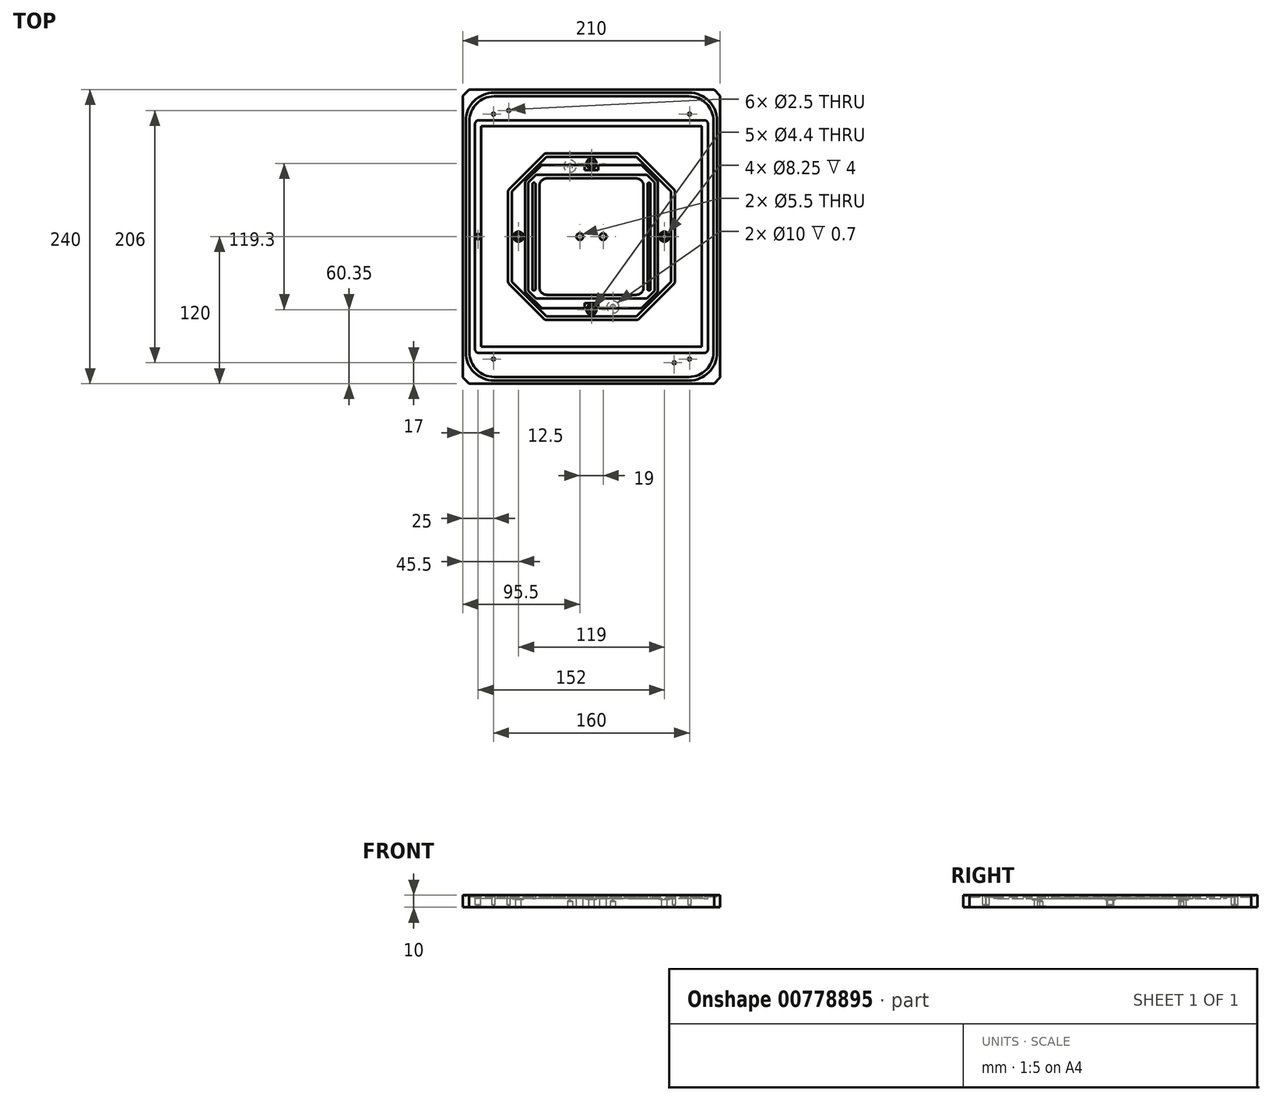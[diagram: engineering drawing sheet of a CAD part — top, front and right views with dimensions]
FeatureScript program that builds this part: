
annotation { "Feature Type Name" : "Feature", "Feature Type Description" : "" }
export const myFeature = defineFeature(function(context is Context, id is Id, definition is map)
    precondition{}
    {
        {
            var Q0;
            Q0=qCreatedBy(makeId("Top.planeOp"),FACE);
            var sketch = newSketch(context, id + "F0", { "sketchPlane" : qUnion([Q0])});
            skLineSegment(sketch, "E0.bottom", {"start": v(105, -120) * mm, "end": v(-105, -120) * mm});
            skLineSegment(sketch, "E0.top", {"start": v(105, 120) * mm, "end": v(-105, 120) * mm});
            skLineSegment(sketch, "E0.left", {"start": v(105, -120) * mm, "end": v(105, 120) * mm});
            skLineSegment(sketch, "E0.right", {"start": v(-105, -120) * mm, "end": v(-105, 120) * mm});
            skPoint(sketch, "E0.middle", {"position": v(0, 0) * mm});
            skSolve(sketch);
        }
        {
            var Q0;
            Q0 = qSketchRegion(id + "F0", true);
            extrude(context, id + "F1", {"entities" : qUnion([Q0]), "depth" : 10 * mm, "offsetDistance" : 25 * mm});
        }
        {
            var Q0;
            Q0=makeQuery(id+"F1.opExtrude","CAP_FACE",FACE,{"disambiguationData":[OSD([sQuery(id+"F0.wireOp",EDGE,"E0.bottom"),sQuery(id+"F0.wireOp",EDGE,"E0.top"),sQuery(id+"F0.wireOp",EDGE,"E0.left"),sQuery(id+"F0.wireOp",EDGE,"E0.right")])],"isStart":false});
            var sketch = newSketch(context, id + "F2", { "sketchPlane" : qUnion([Q0])});
            skPoint(sketch, "E1.middle", {"position": v(0, 0) * mm});
            skLineSegment(sketch, "E2.bottom", {"start": v(79.5, -114.5) * mm, "end": v(-79.5, -114.5) * mm});
            skLineSegment(sketch, "E2.top", {"start": v(79.5, 114.5) * mm, "end": v(-79.5, 114.5) * mm});
            skLineSegment(sketch, "E2.left", {"start": v(99.5, -94.5) * mm, "end": v(99.5, 94.5) * mm});
            skLineSegment(sketch, "E2.right", {"start": v(-99.5, -94.5) * mm, "end": v(-99.5, 94.5) * mm});
            skPoint(sketch, "E3.visualSharp", {"position": v(99.5, 114.5) * mm});
            skArc(sketch, "E3.filletArc", {"start": v(99.5, 94.5) * mm, "mid": v(93.64, 108.64) * mm, "end": v(79.5, 114.5) * mm});
            skPoint(sketch, "E4.visualSharp", {"position": v(-99.5, 114.5) * mm});
            skArc(sketch, "E4.filletArc", {"start": v(-79.5, 114.5) * mm, "mid": v(-93.64, 108.64) * mm, "end": v(-99.5, 94.5) * mm});
            skPoint(sketch, "E5.visualSharp", {"position": v(-99.5, -114.5) * mm});
            skArc(sketch, "E5.filletArc", {"start": v(-99.5, -94.5) * mm, "mid": v(-93.64, -108.64) * mm, "end": v(-79.5, -114.5) * mm});
            skPoint(sketch, "E6.visualSharp", {"position": v(99.5, -114.5) * mm});
            skArc(sketch, "E6.filletArc", {"start": v(79.5, -114.5) * mm, "mid": v(93.64, -108.64) * mm, "end": v(99.5, -94.5) * mm});
            skArc(sketch, "E7.0", {"start": v(102.5, 94.5) * mm, "mid": v(95.76, 110.76) * mm, "end": v(79.5, 117.5) * mm});
            skLineSegment(sketch, "E7.1", {"start": v(102.5, -94.5) * mm, "end": v(102.5, 94.5) * mm});
            skLineSegment(sketch, "E7.2", {"start": v(79.5, 117.5) * mm, "end": v(-79.5, 117.5) * mm});
            skArc(sketch, "E7.3", {"start": v(79.5, -117.5) * mm, "mid": v(95.76, -110.76) * mm, "end": v(102.5, -94.5) * mm});
            skArc(sketch, "E7.4", {"start": v(-79.5, 117.5) * mm, "mid": v(-95.76, 110.76) * mm, "end": v(-102.5, 94.5) * mm});
            skLineSegment(sketch, "E7.5", {"start": v(-102.5, -94.5) * mm, "end": v(-102.5, 94.5) * mm});
            skArc(sketch, "E7.6", {"start": v(-102.5, -94.5) * mm, "mid": v(-95.76, -110.76) * mm, "end": v(-79.5, -117.5) * mm});
            skLineSegment(sketch, "E7.7", {"start": v(79.5, -117.5) * mm, "end": v(-79.5, -117.5) * mm});
            skSolve(sketch);
        }
        {
            var Q0;
            Q0 = qSketchRegion(id + "F2", true);
            extrude(context, id + "F3", {"entities" : qUnion([Q0]), "operationType" : NewBodyOperationType.REMOVE, "oppositeDirection" : true, "depth" : 1.5 * mm, "offsetDistance" : 25 * mm});
        }
        {
            var Q0;
            Q0=makeQuery(id+"F3.boolean.opBoolean","SPLIT",FACE,{"disambiguationData":[TD([makeQuery(id+"F3.opExtrude","SWEPT_FACE",FACE,{"disambiguationData":[OSD([sQuery(id+"F2.wireOp",EDGE,"E2.bottom")])]})])],"derivedFrom":makeQuery(id+"F1.opExtrude","CAP_FACE",FACE,{"disambiguationData":[OSD([sQuery(id+"F0.wireOp",EDGE,"E0.bottom"),sQuery(id+"F0.wireOp",EDGE,"E0.top"),sQuery(id+"F0.wireOp",EDGE,"E0.left"),sQuery(id+"F0.wireOp",EDGE,"E0.right")])],"isStart":false})});
            var sketch = newSketch(context, id + "F4", { "sketchPlane" : qUnion([Q0])});
            skLineSegment(sketch, "E8.bottom", {"start": v(90, -90) * mm, "end": v(-90, -90) * mm});
            skLineSegment(sketch, "E8.top", {"start": v(90, 90) * mm, "end": v(-90, 90) * mm});
            skLineSegment(sketch, "E8.left", {"start": v(90, -90) * mm, "end": v(90, 90) * mm});
            skLineSegment(sketch, "E8.right", {"start": v(-90, -90) * mm, "end": v(-90, 90) * mm});
            skPoint(sketch, "E8.middle", {"position": v(0, 0) * mm});
            skLineSegment(sketch, "E9.0", {"start": v(92, 95) * mm, "end": v(-92, 95) * mm});
            skLineSegment(sketch, "E9.1", {"start": v(95, -92) * mm, "end": v(95, 92) * mm});
            skLineSegment(sketch, "E9.2", {"start": v(92, -95) * mm, "end": v(-92, -95) * mm});
            skLineSegment(sketch, "E9.3", {"start": v(-95, -92) * mm, "end": v(-95, 92) * mm});
            skPoint(sketch, "E10.visualSharp", {"position": v(95, 95) * mm});
            skArc(sketch, "E10.filletArc", {"start": v(95, 92) * mm, "mid": v(94.12, 94.12) * mm, "end": v(92, 95) * mm});
            skPoint(sketch, "E11.visualSharp", {"position": v(-95, 95) * mm});
            skArc(sketch, "E11.filletArc", {"start": v(-92, 95) * mm, "mid": v(-94.12, 94.12) * mm, "end": v(-95, 92) * mm});
            skPoint(sketch, "E12.visualSharp", {"position": v(-95, -95) * mm});
            skArc(sketch, "E12.filletArc", {"start": v(-95, -92) * mm, "mid": v(-94.12, -94.12) * mm, "end": v(-92, -95) * mm});
            skPoint(sketch, "E13.visualSharp", {"position": v(95, -95) * mm});
            skArc(sketch, "E13.filletArc", {"start": v(92, -95) * mm, "mid": v(94.12, -94.12) * mm, "end": v(95, -92) * mm});
            skSolve(sketch);
        }
        {
            var Q0;
            Q0 = qSketchRegion(id + "F4", true);
            extrude(context, id + "F5", {"entities" : qUnion([Q0]), "operationType" : NewBodyOperationType.REMOVE, "oppositeDirection" : true, "depth" : 3 * mm, "offsetDistance" : 25 * mm});
        }
        {
            var Q0;
            Q0=makeQuery(id+"F5.boolean.opBoolean","SPLIT",FACE,{"disambiguationData":[TD([makeQuery(id+"F5.opExtrude","SWEPT_FACE",FACE,{"disambiguationData":[OSD([sQuery(id+"F4.wireOp",EDGE,"E8.bottom")])]})])],"derivedFrom":makeQuery(id+"F3.boolean.opBoolean","SPLIT",FACE,{"disambiguationData":[TD([makeQuery(id+"F3.opExtrude","SWEPT_FACE",FACE,{"disambiguationData":[OSD([sQuery(id+"F2.wireOp",EDGE,"E2.bottom")])]})])],"derivedFrom":makeQuery(id+"F1.opExtrude","CAP_FACE",FACE,{"disambiguationData":[OSD([sQuery(id+"F0.wireOp",EDGE,"E0.bottom"),sQuery(id+"F0.wireOp",EDGE,"E0.top"),sQuery(id+"F0.wireOp",EDGE,"E0.left"),sQuery(id+"F0.wireOp",EDGE,"E0.right")])],"isStart":false})})});
            var sketch = newSketch(context, id + "F6", { "sketchPlane" : qUnion([Q0])});
            skLineSegment(sketch, "E14", {"start": v(-90, 0) * mm, "end": v(90, 0) * mm, "construction": true});
            skLineSegment(sketch, "E15", {"start": v(0, 90) * mm, "end": v(0, -90) * mm, "construction": true});
            skLineSegment(sketch, "E16", {"start": v(-65, 0) * mm, "end": v(-65, 36.72) * mm});
            skLineSegment(sketch, "E17", {"start": v(-65, 36.72) * mm, "end": v(-36.72, 65) * mm});
            skLineSegment(sketch, "E18", {"start": v(-36.72, 65) * mm, "end": v(0, 65) * mm});
            skLineSegment(sketch, "E19.MirrorCS", {"start": v(65, 0) * mm, "end": v(65, 36.72) * mm});
            skLineSegment(sketch, "E20.MirrorCS", {"start": v(36.72, 65) * mm, "end": v(0, 65) * mm});
            skLineSegment(sketch, "E21.MirrorCS", {"start": v(65, 36.72) * mm, "end": v(36.72, 65) * mm});
            skLineSegment(sketch, "E22.MirrorCS", {"start": v(65, 0) * mm, "end": v(65, -36.72) * mm});
            skLineSegment(sketch, "E23.MirrorCS", {"start": v(65, -36.72) * mm, "end": v(36.72, -65) * mm});
            skLineSegment(sketch, "E24.MirrorCS", {"start": v(36.72, -65) * mm, "end": v(0, -65) * mm});
            skLineSegment(sketch, "E25.MirrorCS", {"start": v(-36.72, -65) * mm, "end": v(0, -65) * mm});
            skLineSegment(sketch, "E26.MirrorCS", {"start": v(-65, -36.72) * mm, "end": v(-36.72, -65) * mm});
            skLineSegment(sketch, "E27.MirrorCS", {"start": v(-65, 0) * mm, "end": v(-65, -36.72) * mm});
            skLineSegment(sketch, "E28.0", {"start": v(67.12, 38.84) * mm, "end": v(38.84, 67.12) * mm});
            skLineSegment(sketch, "E28.1", {"start": v(-68, 0) * mm, "end": v(-68, -36.72) * mm});
            skLineSegment(sketch, "E28.2", {"start": v(-68, 0) * mm, "end": v(-68, 36.72) * mm});
            skLineSegment(sketch, "E28.3", {"start": v(-67.12, 38.84) * mm, "end": v(-38.84, 67.12) * mm});
            skLineSegment(sketch, "E28.4", {"start": v(-36.72, 68) * mm, "end": v(0, 68) * mm});
            skLineSegment(sketch, "E28.5", {"start": v(-67.12, -38.84) * mm, "end": v(-38.84, -67.12) * mm});
            skLineSegment(sketch, "E28.6", {"start": v(36.72, 68) * mm, "end": v(0, 68) * mm});
            skLineSegment(sketch, "E28.7", {"start": v(-36.72, -68) * mm, "end": v(0, -68) * mm});
            skLineSegment(sketch, "E28.8", {"start": v(36.72, -68) * mm, "end": v(0, -68) * mm});
            skLineSegment(sketch, "E28.9", {"start": v(67.12, -38.84) * mm, "end": v(38.84, -67.12) * mm});
            skLineSegment(sketch, "E28.10", {"start": v(68, 0) * mm, "end": v(68, -36.72) * mm});
            skLineSegment(sketch, "E28.11", {"start": v(68, 0) * mm, "end": v(68, 36.72) * mm});
            skPoint(sketch, "E29.visualSharp", {"position": v(37.96, 68) * mm});
            skArc(sketch, "E29.filletArc", {"start": v(38.84, 67.12) * mm, "mid": v(37.86, 67.77) * mm, "end": v(36.72, 68) * mm});
            skPoint(sketch, "E30.visualSharp", {"position": v(-37.96, 68) * mm});
            skArc(sketch, "E30.filletArc", {"start": v(-36.72, 68) * mm, "mid": v(-37.86, 67.77) * mm, "end": v(-38.84, 67.12) * mm});
            skPoint(sketch, "E31.visualSharp", {"position": v(-68, 37.96) * mm});
            skArc(sketch, "E31.filletArc", {"start": v(-67.12, 38.84) * mm, "mid": v(-67.77, 37.86) * mm, "end": v(-68, 36.72) * mm});
            skPoint(sketch, "E32.visualSharp", {"position": v(68, 37.96) * mm});
            skArc(sketch, "E32.filletArc", {"start": v(68, 36.72) * mm, "mid": v(67.77, 37.86) * mm, "end": v(67.12, 38.84) * mm});
            skPoint(sketch, "E33.visualSharp", {"position": v(-68, -37.96) * mm});
            skArc(sketch, "E33.filletArc", {"start": v(-68, -36.72) * mm, "mid": v(-67.77, -37.86) * mm, "end": v(-67.12, -38.84) * mm});
            skPoint(sketch, "E34.visualSharp", {"position": v(-37.96, -68) * mm});
            skArc(sketch, "E34.filletArc", {"start": v(-38.84, -67.12) * mm, "mid": v(-37.86, -67.77) * mm, "end": v(-36.72, -68) * mm});
            skPoint(sketch, "E35.visualSharp", {"position": v(37.96, -68) * mm});
            skArc(sketch, "E35.filletArc", {"start": v(36.72, -68) * mm, "mid": v(37.86, -67.77) * mm, "end": v(38.84, -67.12) * mm});
            skPoint(sketch, "E36.visualSharp", {"position": v(68, -37.96) * mm});
            skArc(sketch, "E36.filletArc", {"start": v(67.12, -38.84) * mm, "mid": v(67.77, -37.86) * mm, "end": v(68, -36.72) * mm});
            skSolve(sketch);
        }
        {
            var Q0;
            Q0 = qSketchRegion(id + "F6", true);
            var Q1;
            Q1=makeQuery(id+"F5.boolean.opBoolean","COPY",FACE,{"derivedFrom":makeQuery(id+"F5.opExtrude","CAP_FACE",FACE,{"disambiguationData":[OSD([sQuery(id+"F4.wireOp",EDGE,"E8.bottom"),sQuery(id+"F4.wireOp",EDGE,"E8.top"),sQuery(id+"F4.wireOp",EDGE,"E8.left"),sQuery(id+"F4.wireOp",EDGE,"E8.right"),sQuery(id+"F4.wireOp",EDGE,"E9.0"),sQuery(id+"F4.wireOp",EDGE,"E9.1"),sQuery(id+"F4.wireOp",EDGE,"E9.2"),sQuery(id+"F4.wireOp",EDGE,"E9.3"),sQuery(id+"F4.wireOp",EDGE,"E10.filletArc"),sQuery(id+"F4.wireOp",EDGE,"E11.filletArc"),sQuery(id+"F4.wireOp",EDGE,"E12.filletArc"),sQuery(id+"F4.wireOp",EDGE,"E13.filletArc")])],"isStart":false})});
            extrude(context, id + "F7", {"entities" : qUnion([Q0]), "operationType" : NewBodyOperationType.REMOVE, "endBound" : BoundingType.UP_TO_SURFACE, "oppositeDirection" : true, "depth" : 25 * mm, "endBoundEntityFace" : qUnion([Q1]), "offsetDistance" : 25 * mm});
        }
        {
            var Q0;
            Q0=makeQuery(id+"F7.boolean.opBoolean","SPLIT",FACE,{"disambiguationData":[TD([makeQuery(id+"F7.opExtrude","SWEPT_FACE",FACE,{"disambiguationData":[OSD([sQuery(id+"F6.wireOp",EDGE,"E17")])]})])],"derivedFrom":makeQuery(id+"F5.boolean.opBoolean","SPLIT",FACE,{"disambiguationData":[TD([makeQuery(id+"F5.opExtrude","SWEPT_FACE",FACE,{"disambiguationData":[OSD([sQuery(id+"F4.wireOp",EDGE,"E8.bottom")])]})])],"derivedFrom":makeQuery(id+"F3.boolean.opBoolean","SPLIT",FACE,{"disambiguationData":[TD([makeQuery(id+"F3.opExtrude","SWEPT_FACE",FACE,{"disambiguationData":[OSD([sQuery(id+"F2.wireOp",EDGE,"E2.bottom")])]})])],"derivedFrom":makeQuery(id+"F1.opExtrude","CAP_FACE",FACE,{"disambiguationData":[OSD([sQuery(id+"F0.wireOp",EDGE,"E0.bottom"),sQuery(id+"F0.wireOp",EDGE,"E0.top"),sQuery(id+"F0.wireOp",EDGE,"E0.left"),sQuery(id+"F0.wireOp",EDGE,"E0.right")])],"isStart":false})})})});
            var sketch = newSketch(context, id + "F8", { "sketchPlane" : qUnion([Q0])});
            skLineSegment(sketch, "E37", {"start": v(-65, 0) * mm, "end": v(65, 0) * mm, "construction": true});
            skLineSegment(sketch, "E38", {"start": v(0, 65) * mm, "end": v(0, -65) * mm, "construction": true});
            skLineSegment(sketch, "E39", {"start": v(-51.5, 0) * mm, "end": v(-51.5, 44.14) * mm});
            skLineSegment(sketch, "E40", {"start": v(-51.5, 44.14) * mm, "end": v(-45.14, 50.5) * mm});
            skLineSegment(sketch, "E41", {"start": v(-45.14, 50.5) * mm, "end": v(0, 50.5) * mm});
            skLineSegment(sketch, "E42", {"start": v(-54, 0) * mm, "end": v(-54, 45.17) * mm});
            skLineSegment(sketch, "E43", {"start": v(-54, 45.17) * mm, "end": v(-40.67, 58.5) * mm});
            skLineSegment(sketch, "E44", {"start": v(-40.67, 58.5) * mm, "end": v(-5.5, 58.5) * mm});
            skLineSegment(sketch, "E45", {"start": v(-5.5, 58.5) * mm, "end": v(-5.5, 54.3) * mm});
            skLineSegment(sketch, "E46", {"start": v(-5.5, 54.3) * mm, "end": v(0, 54.3) * mm});
            skLineSegment(sketch, "E47.MirrorCS", {"start": v(5.5, 54.3) * mm, "end": v(0, 54.3) * mm});
            skLineSegment(sketch, "E48.MirrorCS", {"start": v(5.5, 58.5) * mm, "end": v(5.5, 54.3) * mm});
            skLineSegment(sketch, "E49.MirrorCS", {"start": v(40.67, 58.5) * mm, "end": v(5.5, 58.5) * mm});
            skLineSegment(sketch, "E50.MirrorCS", {"start": v(45.14, 50.5) * mm, "end": v(0, 50.5) * mm});
            skLineSegment(sketch, "E51.MirrorCS", {"start": v(54, 45.17) * mm, "end": v(40.67, 58.5) * mm});
            skLineSegment(sketch, "E52.MirrorCS", {"start": v(51.5, 44.14) * mm, "end": v(45.14, 50.5) * mm});
            skLineSegment(sketch, "E53.MirrorCS", {"start": v(54, 0) * mm, "end": v(54, 45.17) * mm});
            skLineSegment(sketch, "E54.MirrorCS", {"start": v(51.5, 0) * mm, "end": v(51.5, 44.14) * mm});
            skLineSegment(sketch, "E55.MirrorCS", {"start": v(54, 0) * mm, "end": v(54, -45.17) * mm});
            skLineSegment(sketch, "E56.MirrorCS", {"start": v(51.5, 0) * mm, "end": v(51.5, -44.14) * mm});
            skLineSegment(sketch, "E57.MirrorCS", {"start": v(51.5, -44.14) * mm, "end": v(45.14, -50.5) * mm});
            skLineSegment(sketch, "E58.MirrorCS", {"start": v(54, -45.17) * mm, "end": v(40.67, -58.5) * mm});
            skLineSegment(sketch, "E59.MirrorCS", {"start": v(40.67, -58.5) * mm, "end": v(5.5, -58.5) * mm});
            skLineSegment(sketch, "E60.MirrorCS", {"start": v(45.14, -50.5) * mm, "end": v(0, -50.5) * mm});
            skLineSegment(sketch, "E61.MirrorCS", {"start": v(5.5, -58.5) * mm, "end": v(5.5, -54.3) * mm});
            skLineSegment(sketch, "E62.MirrorCS", {"start": v(5.5, -54.3) * mm, "end": v(0, -54.3) * mm});
            skLineSegment(sketch, "E63.MirrorCS", {"start": v(-5.5, -54.3) * mm, "end": v(0, -54.3) * mm});
            skLineSegment(sketch, "E64.MirrorCS", {"start": v(-5.5, -58.5) * mm, "end": v(-5.5, -54.3) * mm});
            skLineSegment(sketch, "E65.MirrorCS", {"start": v(-40.67, -58.5) * mm, "end": v(-5.5, -58.5) * mm});
            skLineSegment(sketch, "E66.MirrorCS", {"start": v(-45.14, -50.5) * mm, "end": v(0, -50.5) * mm});
            skLineSegment(sketch, "E67.MirrorCS", {"start": v(-54, -45.17) * mm, "end": v(-40.67, -58.5) * mm});
            skLineSegment(sketch, "E68.MirrorCS", {"start": v(-51.5, -44.14) * mm, "end": v(-45.14, -50.5) * mm});
            skLineSegment(sketch, "E69.MirrorCS", {"start": v(-54, 0) * mm, "end": v(-54, -45.17) * mm});
            skLineSegment(sketch, "E70.MirrorCS", {"start": v(-51.5, 0) * mm, "end": v(-51.5, -44.14) * mm});
            skSolve(sketch);
        }
        {
            var Q0;
            Q0 = qSketchRegion(id + "F8", true);
            var Q1;
            Q1=makeQuery(id+"F5.boolean.opBoolean","COPY",FACE,{"derivedFrom":makeQuery(id+"F5.opExtrude","CAP_FACE",FACE,{"disambiguationData":[OSD([sQuery(id+"F4.wireOp",EDGE,"E8.bottom"),sQuery(id+"F4.wireOp",EDGE,"E8.top"),sQuery(id+"F4.wireOp",EDGE,"E8.left"),sQuery(id+"F4.wireOp",EDGE,"E8.right"),sQuery(id+"F4.wireOp",EDGE,"E9.0"),sQuery(id+"F4.wireOp",EDGE,"E9.1"),sQuery(id+"F4.wireOp",EDGE,"E9.2"),sQuery(id+"F4.wireOp",EDGE,"E9.3"),sQuery(id+"F4.wireOp",EDGE,"E10.filletArc"),sQuery(id+"F4.wireOp",EDGE,"E11.filletArc"),sQuery(id+"F4.wireOp",EDGE,"E12.filletArc"),sQuery(id+"F4.wireOp",EDGE,"E13.filletArc")])],"isStart":false})});
            extrude(context, id + "F9", {"entities" : qUnion([Q0]), "operationType" : NewBodyOperationType.REMOVE, "endBound" : BoundingType.UP_TO_SURFACE, "oppositeDirection" : true, "depth" : 25 * mm, "endBoundEntityFace" : qUnion([Q1]), "offsetDistance" : 25 * mm});
        }
        {
            var Q0;
            Q0=makeQuery(id+"F9.boolean.opBoolean","SPLIT",FACE,{"disambiguationData":[TD([makeQuery(id+"F9.opExtrude","SWEPT_FACE",FACE,{"disambiguationData":[OSD([sQuery(id+"F8.wireOp",EDGE,"E40")])]})])],"derivedFrom":makeQuery(id+"F7.boolean.opBoolean","SPLIT",FACE,{"disambiguationData":[TD([makeQuery(id+"F7.opExtrude","SWEPT_FACE",FACE,{"disambiguationData":[OSD([sQuery(id+"F6.wireOp",EDGE,"E17")])]})])],"derivedFrom":makeQuery(id+"F5.boolean.opBoolean","SPLIT",FACE,{"disambiguationData":[TD([makeQuery(id+"F5.opExtrude","SWEPT_FACE",FACE,{"disambiguationData":[OSD([sQuery(id+"F4.wireOp",EDGE,"E8.bottom")])]})])],"derivedFrom":makeQuery(id+"F3.boolean.opBoolean","SPLIT",FACE,{"disambiguationData":[TD([makeQuery(id+"F3.opExtrude","SWEPT_FACE",FACE,{"disambiguationData":[OSD([sQuery(id+"F2.wireOp",EDGE,"E2.bottom")])]})])],"derivedFrom":makeQuery(id+"F1.opExtrude","CAP_FACE",FACE,{"disambiguationData":[OSD([sQuery(id+"F0.wireOp",EDGE,"E0.bottom"),sQuery(id+"F0.wireOp",EDGE,"E0.top"),sQuery(id+"F0.wireOp",EDGE,"E0.left"),sQuery(id+"F0.wireOp",EDGE,"E0.right")])],"isStart":false})})})})});
            var sketch = newSketch(context, id + "F10", { "sketchPlane" : qUnion([Q0])});
            skLineSegment(sketch, "E71", {"start": v(0, 50.5) * mm, "end": v(0, -50.5) * mm, "construction": true});
            skLineSegment(sketch, "E72.left", {"start": v(-48.2, 42.75) * mm, "end": v(-48.2, -42.75) * mm});
            skLineSegment(sketch, "E72.right", {"start": v(-45.7, 42.75) * mm, "end": v(-45.7, -42.75) * mm});
            skArc(sketch, "E73", {"start": v(-45.7, 42.75) * mm, "mid": v(-46.95, 44) * mm, "end": v(-48.2, 42.75) * mm});
            skArc(sketch, "E74", {"start": v(-48.2, -42.75) * mm, "mid": v(-46.95, -44) * mm, "end": v(-45.7, -42.75) * mm});
            skLineSegment(sketch, "E75", {"start": v(51.5, 0) * mm, "end": v(-51.5, 0) * mm, "construction": true});
            skArc(sketch, "E76.MirrorCS", {"start": v(48.2, -42.75) * mm, "mid": v(46.95, -44) * mm, "end": v(45.7, -42.75) * mm});
            skLineSegment(sketch, "E77.MirrorCS", {"start": v(48.2, 42.75) * mm, "end": v(48.2, -42.75) * mm});
            skLineSegment(sketch, "E78.MirrorCS", {"start": v(45.7, 42.75) * mm, "end": v(45.7, -42.75) * mm});
            skArc(sketch, "E79.MirrorCS", {"start": v(45.7, 42.75) * mm, "mid": v(46.95, 44) * mm, "end": v(48.2, 42.75) * mm});
            skSolve(sketch);
        }
        {
            var Q0;
            Q0 = qSketchRegion(id + "F10", true);
            var Q1;
            Q1=makeQuery(id+"F5.boolean.opBoolean","COPY",FACE,{"derivedFrom":makeQuery(id+"F5.opExtrude","CAP_FACE",FACE,{"disambiguationData":[OSD([sQuery(id+"F4.wireOp",EDGE,"E8.bottom"),sQuery(id+"F4.wireOp",EDGE,"E8.top"),sQuery(id+"F4.wireOp",EDGE,"E8.left"),sQuery(id+"F4.wireOp",EDGE,"E8.right"),sQuery(id+"F4.wireOp",EDGE,"E9.0"),sQuery(id+"F4.wireOp",EDGE,"E9.1"),sQuery(id+"F4.wireOp",EDGE,"E9.2"),sQuery(id+"F4.wireOp",EDGE,"E9.3"),sQuery(id+"F4.wireOp",EDGE,"E10.filletArc"),sQuery(id+"F4.wireOp",EDGE,"E11.filletArc"),sQuery(id+"F4.wireOp",EDGE,"E12.filletArc"),sQuery(id+"F4.wireOp",EDGE,"E13.filletArc")])],"isStart":false})});
            extrude(context, id + "F11", {"entities" : qUnion([Q0]), "operationType" : NewBodyOperationType.REMOVE, "endBound" : BoundingType.UP_TO_SURFACE, "oppositeDirection" : true, "depth" : 25 * mm, "endBoundEntityFace" : qUnion([Q1]), "offsetDistance" : 25 * mm});
        }
        {
            var Q0;
            Q0=makeQuery(id+"F9.boolean.opBoolean","SPLIT",FACE,{"disambiguationData":[TD([makeQuery(id+"F9.opExtrude","SWEPT_FACE",FACE,{"disambiguationData":[OSD([sQuery(id+"F8.wireOp",EDGE,"E40")])]})])],"derivedFrom":makeQuery(id+"F7.boolean.opBoolean","SPLIT",FACE,{"disambiguationData":[TD([makeQuery(id+"F7.opExtrude","SWEPT_FACE",FACE,{"disambiguationData":[OSD([sQuery(id+"F6.wireOp",EDGE,"E17")])]})])],"derivedFrom":makeQuery(id+"F5.boolean.opBoolean","SPLIT",FACE,{"disambiguationData":[TD([makeQuery(id+"F5.opExtrude","SWEPT_FACE",FACE,{"disambiguationData":[OSD([sQuery(id+"F4.wireOp",EDGE,"E8.bottom")])]})])],"derivedFrom":makeQuery(id+"F3.boolean.opBoolean","SPLIT",FACE,{"disambiguationData":[TD([makeQuery(id+"F3.opExtrude","SWEPT_FACE",FACE,{"disambiguationData":[OSD([sQuery(id+"F2.wireOp",EDGE,"E2.bottom")])]})])],"derivedFrom":makeQuery(id+"F1.opExtrude","CAP_FACE",FACE,{"disambiguationData":[OSD([sQuery(id+"F0.wireOp",EDGE,"E0.bottom"),sQuery(id+"F0.wireOp",EDGE,"E0.top"),sQuery(id+"F0.wireOp",EDGE,"E0.left"),sQuery(id+"F0.wireOp",EDGE,"E0.right")])],"isStart":false})})})})});
            var sketch = newSketch(context, id + "F12", { "sketchPlane" : qUnion([Q0])});
            skLineSegment(sketch, "E80.bottom", {"start": v(36.5, -47.5) * mm, "end": v(-36.5, -47.5) * mm});
            skLineSegment(sketch, "E80.top", {"start": v(36.5, 47.5) * mm, "end": v(-36.5, 47.5) * mm});
            skLineSegment(sketch, "E80.left", {"start": v(42.5, -41.5) * mm, "end": v(42.5, 41.5) * mm});
            skLineSegment(sketch, "E80.right", {"start": v(-42.5, -41.5) * mm, "end": v(-42.5, 41.5) * mm});
            skPoint(sketch, "E80.middle", {"position": v(0, 0) * mm});
            skPoint(sketch, "E81.visualSharp", {"position": v(42.5, 47.5) * mm});
            skArc(sketch, "E81.filletArc", {"start": v(42.5, 41.5) * mm, "mid": v(40.74, 45.74) * mm, "end": v(36.5, 47.5) * mm});
            skPoint(sketch, "E82.visualSharp", {"position": v(-42.5, 47.5) * mm});
            skArc(sketch, "E82.filletArc", {"start": v(-36.5, 47.5) * mm, "mid": v(-40.74, 45.74) * mm, "end": v(-42.5, 41.5) * mm});
            skPoint(sketch, "E83.visualSharp", {"position": v(-42.5, -47.5) * mm});
            skArc(sketch, "E83.filletArc", {"start": v(-42.5, -41.5) * mm, "mid": v(-40.74, -45.74) * mm, "end": v(-36.5, -47.5) * mm});
            skPoint(sketch, "E84.visualSharp", {"position": v(42.5, -47.5) * mm});
            skArc(sketch, "E84.filletArc", {"start": v(36.5, -47.5) * mm, "mid": v(40.74, -45.74) * mm, "end": v(42.5, -41.5) * mm});
            skSolve(sketch);
        }
        {
            var Q0;
            Q0 = qSketchRegion(id + "F12", true);
            extrude(context, id + "F13", {"entities" : qUnion([Q0]), "operationType" : NewBodyOperationType.REMOVE, "oppositeDirection" : true, "depth" : 2 * mm, "offsetDistance" : 25 * mm});
        }
        {
            var Q0;
            Q0=makeQuery(id+"F13.boolean.opBoolean","COPY",FACE,{"derivedFrom":makeQuery(id+"F13.opExtrude","CAP_FACE",FACE,{"disambiguationData":[OSD([sQuery(id+"F12.wireOp",EDGE,"E80.bottom"),sQuery(id+"F12.wireOp",EDGE,"E80.top"),sQuery(id+"F12.wireOp",EDGE,"E80.left"),sQuery(id+"F12.wireOp",EDGE,"E80.right"),sQuery(id+"F12.wireOp",EDGE,"E81.filletArc"),sQuery(id+"F12.wireOp",EDGE,"E82.filletArc"),sQuery(id+"F12.wireOp",EDGE,"E83.filletArc"),sQuery(id+"F12.wireOp",EDGE,"E84.filletArc")])],"isStart":false})});
            var sketch = newSketch(context, id + "F14", { "sketchPlane" : qUnion([Q0])});
            skLineSegment(sketch, "E85", {"start": v(-9.5, 0) * mm, "end": v(0, 0) * mm, "construction": true});
            skLineSegment(sketch, "E86", {"start": v(0, 0) * mm, "end": v(9.5, 0) * mm, "construction": true});
            skSolve(sketch);
        }
        {
            var Q0;
            Q0=sQuery(id+"F14.wireOp",VERTEX,"E85.start");
            var Q1;
            Q1=sQuery(id+"F14.wireOp",VERTEX,"E86.end");
            var Q2;
            Q2=makeQuery(id+"F1.opExtrude","SWEPT_BODY",BODY,{"disambiguationData":[OSD([sQuery(id+"F0.wireOp",EDGE,"E0.bottom"),sQuery(id+"F0.wireOp",EDGE,"E0.top"),sQuery(id+"F0.wireOp",EDGE,"E0.left"),sQuery(id+"F0.wireOp",EDGE,"E0.right")])]});
            hole(context, id + "F15", {"style" : HoleStyle.SIMPLE, "endStyle" : HoleEndStyle.THROUGH, "standardTappedOrClearance" : lookupTablePath({ "standard" : "ISO", "fit" : "Normal", "size" : "M5", "type" : "Clearance" }), "standardBlindInLast" : lookupTablePath({ "fit" : "Standard", "standard" : "ISO", "size" : "M5", "type" : "Clearance" }), "holeDiameter" : 5.5 * mm, "majorDiameter" : 5 * mm, "isTappedThrough" : true, "tappedDepth" : 12 * mm, "tapClearance" : 3, "locations" : qUnion([Q0, Q1]), "scope" : qUnion([Q2])});
        }
        {
            var Q0;
            {var subQ2=makeQuery(id+"F7.opExtrude","SWEPT_FACE",FACE,{"disambiguationData":[OSD([sQuery(id+"F6.wireOp",EDGE,"E17")])]});Q0=makeQuery(id+"F9.boolean.opBoolean","SPLIT",FACE,{"disambiguationData":[TD([makeQuery(id+"F7.boolean.opBoolean","COPY",FACE,{"derivedFrom":subQ2})])],"derivedFrom":makeQuery(id+"F7.boolean.opBoolean","SPLIT",FACE,{"disambiguationData":[TD([subQ2])],"derivedFrom":makeQuery(id+"F5.boolean.opBoolean","SPLIT",FACE,{"disambiguationData":[TD([makeQuery(id+"F5.opExtrude","SWEPT_FACE",FACE,{"disambiguationData":[OSD([sQuery(id+"F4.wireOp",EDGE,"E8.bottom")])]})])],"derivedFrom":makeQuery(id+"F3.boolean.opBoolean","SPLIT",FACE,{"disambiguationData":[TD([makeQuery(id+"F3.opExtrude","SWEPT_FACE",FACE,{"disambiguationData":[OSD([sQuery(id+"F2.wireOp",EDGE,"E2.bottom")])]})])],"derivedFrom":makeQuery(id+"F1.opExtrude","CAP_FACE",FACE,{"disambiguationData":[OSD([sQuery(id+"F0.wireOp",EDGE,"E0.bottom"),sQuery(id+"F0.wireOp",EDGE,"E0.top"),sQuery(id+"F0.wireOp",EDGE,"E0.left"),sQuery(id+"F0.wireOp",EDGE,"E0.right")])],"isStart":false})})})})});}
            var sketch = newSketch(context, id + "F16", { "sketchPlane" : qUnion([Q0])});
            skLineSegment(sketch, "E87", {"start": v(0, 65) * mm, "end": v(0, 54.3) * mm, "construction": true});
            skLineSegment(sketch, "E88", {"start": v(-42.07, 59.65) * mm, "end": v(42.07, 59.65) * mm, "construction": true});
            skPoint(sketch, "E88.startSnap0", {"position": v(0, 59.65) * mm});
            skLineSegment(sketch, "E89", {"start": v(0, -54.3) * mm, "end": v(0, -65) * mm, "construction": true});
            skLineSegment(sketch, "E90", {"start": v(-42.07, -59.65) * mm, "end": v(42.07, -59.65) * mm, "construction": true});
            skPoint(sketch, "E90.startSnap0", {"position": v(0, -59.65) * mm});
            skLineSegment(sketch, "E91", {"start": v(-65, 0) * mm, "end": v(-54, 0) * mm, "construction": true});
            skLineSegment(sketch, "E92", {"start": v(-59.5, 42.22) * mm, "end": v(-59.5, -42.22) * mm, "construction": true});
            skPoint(sketch, "E92.startSnap0", {"position": v(-59.5, 0) * mm});
            skLineSegment(sketch, "E93", {"start": v(54, 0) * mm, "end": v(65, 0) * mm, "construction": true});
            skLineSegment(sketch, "E94", {"start": v(59.5, 42.22) * mm, "end": v(59.5, -42.22) * mm, "construction": true});
            skPoint(sketch, "E94.startSnap0", {"position": v(59.5, 0) * mm});
            skLineSegment(sketch, "E95.bottom", {"start": v(80, -100) * mm, "end": v(-80, -100) * mm, "construction": true});
            skLineSegment(sketch, "E95.top", {"start": v(80, 100) * mm, "end": v(-80, 100) * mm, "construction": true});
            skLineSegment(sketch, "E95.left", {"start": v(80, -100) * mm, "end": v(80, 100) * mm, "construction": true});
            skLineSegment(sketch, "E95.right", {"start": v(-80, -100) * mm, "end": v(-80, 100) * mm, "construction": true});
            skPoint(sketch, "E95.middle", {"position": v(0, 0) * mm});
            skLineSegment(sketch, "E96.bottom", {"start": v(67.5, -103) * mm, "end": v(-67.5, -103) * mm, "construction": true});
            skLineSegment(sketch, "E96.top", {"start": v(67.5, 103) * mm, "end": v(-67.5, 103) * mm, "construction": true});
            skLineSegment(sketch, "E96.left", {"start": v(67.5, -103) * mm, "end": v(67.5, 103) * mm, "construction": true});
            skLineSegment(sketch, "E96.right", {"start": v(-67.5, -103) * mm, "end": v(-67.5, 103) * mm, "construction": true});
            skSolve(sketch);
        }
        {
            var Q0;
            Q0=sQuery(id+"F16.wireOp",VERTEX,"E88.startSnap0");
            var Q1;
            Q1=sQuery(id+"F16.wireOp",VERTEX,"E94.startSnap0");
            var Q2;
            Q2=sQuery(id+"F16.wireOp",VERTEX,"E90.startSnap0");
            var Q3;
            Q3=sQuery(id+"F16.wireOp",VERTEX,"E92.startSnap0");
            var Q4;
            Q4=makeQuery(id+"F1.opExtrude","SWEPT_BODY",BODY,{"disambiguationData":[OSD([sQuery(id+"F0.wireOp",EDGE,"E0.bottom"),sQuery(id+"F0.wireOp",EDGE,"E0.top"),sQuery(id+"F0.wireOp",EDGE,"E0.left"),sQuery(id+"F0.wireOp",EDGE,"E0.right")])]});
            hole(context, id + "F17", {"style" : HoleStyle.C_BORE, "endStyle" : HoleEndStyle.THROUGH, "standardTappedOrClearance" : lookupTablePath({ "standard" : "ISO", "fit" : "Normal", "size" : "M4", "type" : "Clearance" }), "standardBlindInLast" : lookupTablePath({ "fit" : "Standard", "standard" : "ISO", "size" : "M4", "type" : "Clearance" }), "holeDiameter" : 4.4 * mm, "cBoreDiameter" : 8.25 * mm, "cBoreDepth" : 4 * mm, "majorDiameter" : 5 * mm, "isTappedThrough" : true, "tappedDepth" : 12 * mm, "tapClearance" : 3, "locations" : qUnion([Q0, Q1, Q2, Q3]), "scope" : qUnion([Q4])});
        }
        {
            var Q0;
            Q0=sQuery(id+"F16.wireOp",VERTEX,"E95.top.end");
            var Q1;
            Q1=sQuery(id+"F16.wireOp",VERTEX,"E96.top.end");
            var Q2;
            Q2=sQuery(id+"F16.wireOp",VERTEX,"E95.top.start");
            var Q3;
            Q3=sQuery(id+"F16.wireOp",VERTEX,"E95.bottom.end");
            var Q4;
            Q4=sQuery(id+"F16.wireOp",VERTEX,"E95.bottom.start");
            var Q5;
            Q5=sQuery(id+"F16.wireOp",VERTEX,"E96.bottom.start");
            var Q6;
            Q6=makeQuery(id+"F1.opExtrude","SWEPT_BODY",BODY,{"disambiguationData":[OSD([sQuery(id+"F0.wireOp",EDGE,"E0.bottom"),sQuery(id+"F0.wireOp",EDGE,"E0.top"),sQuery(id+"F0.wireOp",EDGE,"E0.left"),sQuery(id+"F0.wireOp",EDGE,"E0.right")])]});
            hole(context, id + "F18", {"style" : HoleStyle.SIMPLE, "endStyle" : HoleEndStyle.BLIND, "standardTappedOrClearance" : lookupTablePath({ "standard" : "ISO", "engagement" : "75%", "pitch" : "0.5 mm", "size" : "M3", "type" : "Tapped" }), "standardBlindInLast" : lookupTablePath({ "standard" : "ISO", "engagement" : "75%", "pitch" : "0.5 mm", "size" : "M3", "type" : "Tapped" }), "holeDiameter" : 2.5 * mm, "majorDiameter" : 3 * mm, "showTappedDepth" : true, "holeDepth" : 8 * mm, "isTappedThrough" : true, "tappedDepth" : 6.5 * mm, "tapClearance" : 3, "locations" : qUnion([Q0, Q1, Q2, Q3, Q4, Q5]), "scope" : qUnion([Q6])});
        }
        {
            var Q0;
            Q0=makeQuery(id+"F5.boolean.opBoolean","COPY",FACE,{"derivedFrom":makeQuery(id+"F5.opExtrude","CAP_FACE",FACE,{"disambiguationData":[OSD([sQuery(id+"F4.wireOp",EDGE,"E8.bottom"),sQuery(id+"F4.wireOp",EDGE,"E8.top"),sQuery(id+"F4.wireOp",EDGE,"E8.left"),sQuery(id+"F4.wireOp",EDGE,"E8.right"),sQuery(id+"F4.wireOp",EDGE,"E9.0"),sQuery(id+"F4.wireOp",EDGE,"E9.1"),sQuery(id+"F4.wireOp",EDGE,"E9.2"),sQuery(id+"F4.wireOp",EDGE,"E9.3"),sQuery(id+"F4.wireOp",EDGE,"E10.filletArc"),sQuery(id+"F4.wireOp",EDGE,"E11.filletArc"),sQuery(id+"F4.wireOp",EDGE,"E12.filletArc"),sQuery(id+"F4.wireOp",EDGE,"E13.filletArc")])],"isStart":false})});
            var sketch = newSketch(context, id + "F19", { "sketchPlane" : qUnion([Q0])});
            skLineSegment(sketch, "E97", {"start": v(-95, 0) * mm, "end": v(-90, 0) * mm, "construction": true});
            skPoint(sketch, "E98", {"position": v(-92.5, 0) * mm});
            skSolve(sketch);
        }
        {
            var Q0;
            Q0=sQuery(id+"F19.wireOp",VERTEX,"E98");
            var Q1;
            Q1=makeQuery(id+"F1.opExtrude","SWEPT_BODY",BODY,{"disambiguationData":[OSD([sQuery(id+"F0.wireOp",EDGE,"E0.bottom"),sQuery(id+"F0.wireOp",EDGE,"E0.top"),sQuery(id+"F0.wireOp",EDGE,"E0.left"),sQuery(id+"F0.wireOp",EDGE,"E0.right")])]});
            hole(context, id + "F20", {"style" : HoleStyle.SIMPLE, "endStyle" : HoleEndStyle.BLIND, "standardTappedOrClearance" : lookupTablePath({ "standard" : "ISO", "fit" : "Normal", "size" : "M4", "type" : "Clearance" }), "standardBlindInLast" : lookupTablePath({ "fit" : "Standard", "standard" : "ISO", "size" : "M4", "type" : "Clearance" }), "holeDiameter" : 4.4 * mm, "majorDiameter" : 3 * mm, "holeDepth" : 5 * mm, "isTappedThrough" : true, "tappedDepth" : 6.5 * mm, "tapClearance" : 3, "locations" : qUnion([Q0]), "scope" : qUnion([Q1])});
        }
        {
            var Q0;
            Q0=makeQuery(id+"F1.opExtrude","CAP_FACE",FACE,{"disambiguationData":[OSD([sQuery(id+"F0.wireOp",EDGE,"E0.bottom"),sQuery(id+"F0.wireOp",EDGE,"E0.top"),sQuery(id+"F0.wireOp",EDGE,"E0.left"),sQuery(id+"F0.wireOp",EDGE,"E0.right")])],"isStart":true});
            var sketch = newSketch(context, id + "F21", { "sketchPlane" : qUnion([Q0])});
            skLineSegment(sketch, "E99.bottom", {"start": v(-17.5, 57.5) * mm, "end": v(17.5, 57.5) * mm, "construction": true});
            skLineSegment(sketch, "E99.top", {"start": v(-17.5, -57.5) * mm, "end": v(17.5, -57.5) * mm, "construction": true});
            skLineSegment(sketch, "E99.left", {"start": v(-17.5, 57.5) * mm, "end": v(-17.5, -57.5) * mm, "construction": true});
            skLineSegment(sketch, "E99.right", {"start": v(17.5, 57.5) * mm, "end": v(17.5, -57.5) * mm, "construction": true});
            skPoint(sketch, "E99.middle", {"position": v(0, 0) * mm});
            skSolve(sketch);
        }
        {
            var Q0;
            Q0=sQuery(id+"F21.wireOp",VERTEX,"E99.top.start");
            var Q1;
            Q1=sQuery(id+"F21.wireOp",VERTEX,"E99.bottom.end");
            var Q2;
            Q2=makeQuery(id+"F1.opExtrude","SWEPT_BODY",BODY,{"disambiguationData":[OSD([sQuery(id+"F0.wireOp",EDGE,"E0.bottom"),sQuery(id+"F0.wireOp",EDGE,"E0.top"),sQuery(id+"F0.wireOp",EDGE,"E0.left"),sQuery(id+"F0.wireOp",EDGE,"E0.right")])]});
            hole(context, id + "F22", {"style" : HoleStyle.C_BORE, "endStyle" : HoleEndStyle.BLIND, "holeDiameter" : 4.2 * mm, "cBoreDiameter" : 10 * mm, "cBoreDepth" : 0.7 * mm, "majorDiameter" : 5 * mm, "holeDepth" : 5 * mm, "isTappedThrough" : true, "tappedDepth" : 6.5 * mm, "tapClearance" : 3, "locations" : qUnion([Q0, Q1]), "scope" : qUnion([Q2])});
        }
        {
            var Q0;
            Q0=makeQuery(id+"F1.opExtrude","SWEPT_EDGE",EDGE,{"disambiguationData":[OSD([sQuery(id+"F0.wireOp",EDGE,"E0.top"),sQuery(id+"F0.wireOp",EDGE,"E0.right")])]});
            var Q1;
            Q1=makeQuery(id+"F1.opExtrude","SWEPT_EDGE",EDGE,{"disambiguationData":[OSD([sQuery(id+"F0.wireOp",EDGE,"E0.top"),sQuery(id+"F0.wireOp",EDGE,"E0.left")])]});
            var Q2;
            Q2=makeQuery(id+"F1.opExtrude","SWEPT_EDGE",EDGE,{"disambiguationData":[OSD([sQuery(id+"F0.wireOp",EDGE,"E0.bottom"),sQuery(id+"F0.wireOp",EDGE,"E0.right")])]});
            var Q3;
            Q3=makeQuery(id+"F1.opExtrude","SWEPT_EDGE",EDGE,{"disambiguationData":[OSD([sQuery(id+"F0.wireOp",EDGE,"E0.bottom"),sQuery(id+"F0.wireOp",EDGE,"E0.left")])]});
            chamfer(context, id + "F23", {"entities" : qUnion([Q0, Q1, Q2, Q3]), "width" : 5 * mm, "tangentPropagation" : true});
        }
        {
            var Q0;
            Q0=makeQuery(id+"F9.boolean.opBoolean","COPY",EDGE,{"derivedFrom":makeQuery(id+"F9.opExtrude","SWEPT_EDGE",EDGE,{"disambiguationData":[OSD([sQuery(id+"F8.wireOp",EDGE,"E44"),sQuery(id+"F8.wireOp",EDGE,"E45")])]})});
            var Q1;
            Q1=makeQuery(id+"F9.boolean.opBoolean","COPY",EDGE,{"derivedFrom":makeQuery(id+"F9.opExtrude","SWEPT_EDGE",EDGE,{"disambiguationData":[OSD([sQuery(id+"F8.wireOp",EDGE,"E48.MirrorCS"),sQuery(id+"F8.wireOp",EDGE,"E49.MirrorCS")])]})});
            var Q2;
            Q2=makeQuery(id+"F9.boolean.opBoolean","COPY",EDGE,{"derivedFrom":makeQuery(id+"F9.opExtrude","SWEPT_EDGE",EDGE,{"disambiguationData":[OSD([sQuery(id+"F8.wireOp",EDGE,"E59.MirrorCS"),sQuery(id+"F8.wireOp",EDGE,"E61.MirrorCS")])]})});
            var Q3;
            Q3=makeQuery(id+"F9.boolean.opBoolean","COPY",EDGE,{"derivedFrom":makeQuery(id+"F9.opExtrude","SWEPT_EDGE",EDGE,{"disambiguationData":[OSD([sQuery(id+"F8.wireOp",EDGE,"E64.MirrorCS"),sQuery(id+"F8.wireOp",EDGE,"E65.MirrorCS")])]})});
            fillet(context, id + "F24", {"entities" : qUnion([Q0, Q1, Q2, Q3]), "radius" : 1.5 * mm, "tangentPropagation" : true, "allowEdgeOverflow" : false});
        }
        {
            var Q0;
            Q0=makeQuery(id+"F9.boolean.opBoolean","COPY",EDGE,{"derivedFrom":makeQuery(id+"F9.opExtrude","SWEPT_EDGE",EDGE,{"disambiguationData":[OSD([sQuery(id+"F8.wireOp",EDGE,"E49.MirrorCS"),sQuery(id+"F8.wireOp",EDGE,"E51.MirrorCS")])]})});
            var Q1;
            Q1=makeQuery(id+"F9.boolean.opBoolean","COPY",EDGE,{"derivedFrom":makeQuery(id+"F9.opExtrude","SWEPT_EDGE",EDGE,{"disambiguationData":[OSD([sQuery(id+"F8.wireOp",EDGE,"E43"),sQuery(id+"F8.wireOp",EDGE,"E44")])]})});
            var Q2;
            Q2=makeQuery(id+"F9.boolean.opBoolean","COPY",EDGE,{"derivedFrom":makeQuery(id+"F9.opExtrude","SWEPT_EDGE",EDGE,{"disambiguationData":[OSD([sQuery(id+"F8.wireOp",EDGE,"E42"),sQuery(id+"F8.wireOp",EDGE,"E43")])]})});
            var Q3;
            Q3=makeQuery(id+"F9.boolean.opBoolean","COPY",EDGE,{"derivedFrom":makeQuery(id+"F9.opExtrude","SWEPT_EDGE",EDGE,{"disambiguationData":[OSD([sQuery(id+"F8.wireOp",EDGE,"E67.MirrorCS"),sQuery(id+"F8.wireOp",EDGE,"E69.MirrorCS")])]})});
            var Q4;
            Q4=makeQuery(id+"F9.boolean.opBoolean","COPY",EDGE,{"derivedFrom":makeQuery(id+"F9.opExtrude","SWEPT_EDGE",EDGE,{"disambiguationData":[OSD([sQuery(id+"F8.wireOp",EDGE,"E65.MirrorCS"),sQuery(id+"F8.wireOp",EDGE,"E67.MirrorCS")])]})});
            var Q5;
            Q5=makeQuery(id+"F9.boolean.opBoolean","COPY",EDGE,{"derivedFrom":makeQuery(id+"F9.opExtrude","SWEPT_EDGE",EDGE,{"disambiguationData":[OSD([sQuery(id+"F8.wireOp",EDGE,"E58.MirrorCS"),sQuery(id+"F8.wireOp",EDGE,"E59.MirrorCS")])]})});
            var Q6;
            Q6=makeQuery(id+"F9.boolean.opBoolean","COPY",EDGE,{"derivedFrom":makeQuery(id+"F9.opExtrude","SWEPT_EDGE",EDGE,{"disambiguationData":[OSD([sQuery(id+"F8.wireOp",EDGE,"E55.MirrorCS"),sQuery(id+"F8.wireOp",EDGE,"E58.MirrorCS")])]})});
            var Q7;
            Q7=makeQuery(id+"F9.boolean.opBoolean","COPY",EDGE,{"derivedFrom":makeQuery(id+"F9.opExtrude","SWEPT_EDGE",EDGE,{"disambiguationData":[OSD([sQuery(id+"F8.wireOp",EDGE,"E51.MirrorCS"),sQuery(id+"F8.wireOp",EDGE,"E53.MirrorCS")])]})});
            fillet(context, id + "F25", {"entities" : qUnion([Q0, Q1, Q2, Q3, Q4, Q5, Q6, Q7]), "radius" : 2 * mm, "tangentPropagation" : true, "allowEdgeOverflow" : false});
        }
    });
